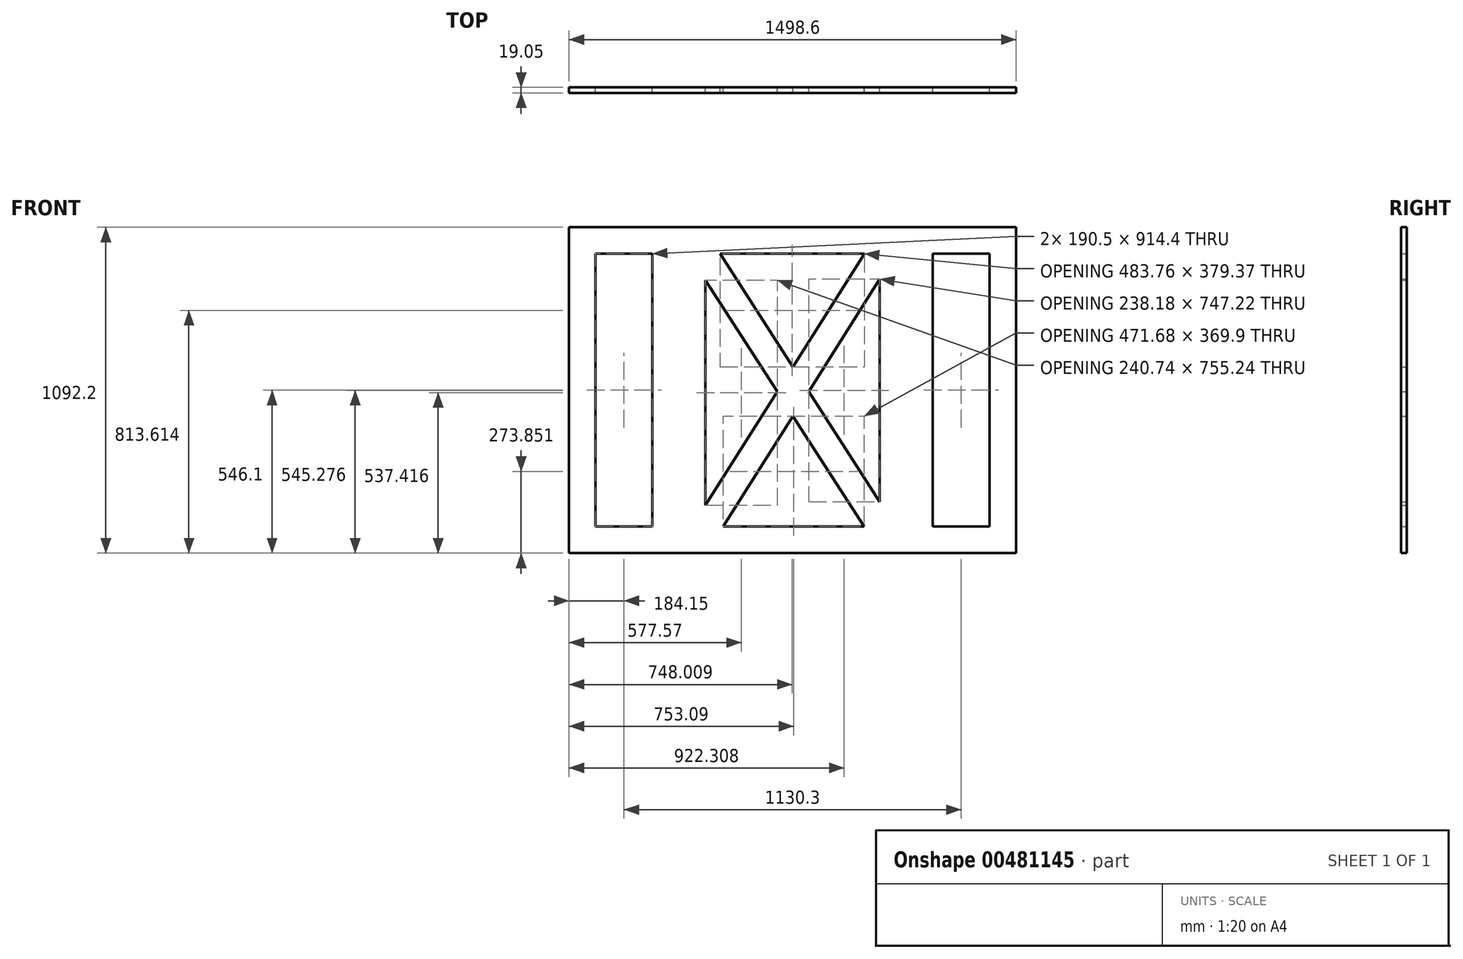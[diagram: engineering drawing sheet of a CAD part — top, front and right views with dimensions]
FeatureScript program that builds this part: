
annotation { "Feature Type Name" : "Feature", "Feature Type Description" : "" }
export const myFeature = defineFeature(function(context is Context, id is Id, definition is map)
    precondition{}
    {
        {
            var Q0;
            Q0=qCreatedBy(makeId("Front.planeOp"),FACE);
            var sketch = newSketch(context, id + "F0", { "sketchPlane" : qUnion([Q0])});
            skPoint(sketch, "E0.middle", {"position": v(0, 0) * mm});
            skLineSegment(sketch, "E1", {"start": v(-749.3, 546.1) * mm, "end": v(-749.3, -546.1) * mm});
            skLineSegment(sketch, "E2", {"start": v(-381, 546.1) * mm, "end": v(-381, -546.1) * mm});
            skLineSegment(sketch, "E3", {"start": v(749.3, 546.1) * mm, "end": v(749.3, -546.1) * mm});
            skLineSegment(sketch, "E4", {"start": v(381, 546.1) * mm, "end": v(381, -546.1) * mm});
            skLineSegment(sketch, "E5.bottom", {"start": v(-660.4, 457.2) * mm, "end": v(-469.9, 457.2) * mm});
            skLineSegment(sketch, "E5.top", {"start": v(-660.4, -457.2) * mm, "end": v(-469.9, -457.2) * mm});
            skLineSegment(sketch, "E5.left", {"start": v(-660.4, 457.2) * mm, "end": v(-660.4, -457.2) * mm});
            skLineSegment(sketch, "E5.right", {"start": v(-469.9, 457.2) * mm, "end": v(-469.9, -457.2) * mm});
            skLineSegment(sketch, "E6.MirrorCS", {"start": v(660.4, 457.2) * mm, "end": v(469.9, 457.2) * mm});
            skLineSegment(sketch, "E7.MirrorCS", {"start": v(660.4, 457.2) * mm, "end": v(660.4, -457.2) * mm});
            skLineSegment(sketch, "E8.MirrorCS", {"start": v(660.4, -457.2) * mm, "end": v(469.9, -457.2) * mm});
            skLineSegment(sketch, "E9.MirrorCS", {"start": v(469.9, 457.2) * mm, "end": v(469.9, -457.2) * mm});
            skLineSegment(sketch, "E10.bottom", {"start": v(-292.1, 457.2) * mm, "end": v(292.1, 457.2) * mm});
            skLineSegment(sketch, "E10.top", {"start": v(-292.1, -457.2) * mm, "end": v(292.1, -457.2) * mm});
            skLineSegment(sketch, "E10.left", {"start": v(-292.1, 457.2) * mm, "end": v(-292.1, -457.2) * mm});
            skLineSegment(sketch, "E10.right", {"start": v(292.1, 457.2) * mm, "end": v(292.1, -457.2) * mm});
            skLineSegment(sketch, "E11.0", {"start": v(-243.17, 457.2) * mm, "end": v(292.1, -374.43) * mm});
            skLineSegment(sketch, "E12.0", {"start": v(-292.1, 368.94) * mm, "end": v(239.63, -457.2) * mm});
            skLineSegment(sketch, "E13.0", {"start": v(240.59, 457.2) * mm, "end": v(-292.1, -386.3) * mm});
            skLineSegment(sketch, "E14.0", {"start": v(292.1, 372.79) * mm, "end": v(-232.05, -457.2) * mm});
            skLineSegment(sketch, "E15", {"start": v(-749.3, 546.1) * mm, "end": v(749.3, 546.1) * mm});
            skLineSegment(sketch, "E16", {"start": v(-749.3, -546.1) * mm, "end": v(749.3, -546.1) * mm});
            skSolve(sketch);
        }
        {
            var Q0;
            Q0 = qSketchRegion(id + "F0", true);
            var Q1;
            {var subQ1=sQuery(id+"F0.wireOp",EDGE,"E10.bottom");var subQ5=sQuery(id+"F0.wireOp",EDGE,"E10.left");var subQ6=makeQuery(id+"F0.imprint","INTERSECT",VERTEX,{"derivedFrom":[subQ1,subQ5]});Q1=makeQuery(id+"F0.imprint","IMPRINT",FACE,{"disambiguationData":[TD([[makeQuery(id+"F0.imprint","IMPRINT",EDGE,{"disambiguationData":[TD([[subQ6,-1.0]])],"derivedFrom":subQ1}),-1.0]])]});}
            var Q2;
            {var subQ1=sQuery(id+"F0.wireOp",EDGE,"E10.bottom");var subQ7=sQuery(id+"F0.wireOp",EDGE,"E10.right");var subQ8=makeQuery(id+"F0.imprint","INTERSECT",VERTEX,{"derivedFrom":[subQ1,subQ7]});Q2=makeQuery(id+"F0.imprint","IMPRINT",FACE,{"disambiguationData":[TD([[makeQuery(id+"F0.imprint","IMPRINT",EDGE,{"disambiguationData":[TD([[subQ8,1.0]])],"derivedFrom":subQ1}),-1.0]])]});}
            var Q3;
            {var subQ0=sQuery(id+"F0.wireOp",EDGE,"E13.0");var subQ1=sQuery(id+"F0.wireOp",EDGE,"E11.0");var subQ2=makeQuery(id+"F0.imprint","INTERSECT",VERTEX,{"derivedFrom":[subQ1,subQ0]});Q3=makeQuery(id+"F0.imprint","IMPRINT",FACE,{"disambiguationData":[TD([[makeQuery(id+"F0.imprint","IMPRINT",EDGE,{"disambiguationData":[TD([[subQ2,-1.0]])],"derivedFrom":subQ1}),-1.0]])]});}
            var Q4;
            {var subQ1=sQuery(id+"F0.wireOp",EDGE,"E10.left");var subQ7=sQuery(id+"F0.wireOp",EDGE,"E10.top");var subQ8=makeQuery(id+"F0.imprint","INTERSECT",VERTEX,{"derivedFrom":[subQ7,subQ1]});Q4=makeQuery(id+"F0.imprint","IMPRINT",FACE,{"disambiguationData":[TD([[makeQuery(id+"F0.imprint","IMPRINT",EDGE,{"disambiguationData":[TD([[subQ8,-1.0]])],"derivedFrom":subQ7}),1.0]])]});}
            var Q5;
            {var subQ1=sQuery(id+"F0.wireOp",EDGE,"E10.top");var subQ6=sQuery(id+"F0.wireOp",EDGE,"E10.right");var subQ9=makeQuery(id+"F0.imprint","INTERSECT",VERTEX,{"derivedFrom":[subQ1,subQ6]});Q5=makeQuery(id+"F0.imprint","IMPRINT",FACE,{"disambiguationData":[TD([[makeQuery(id+"F0.imprint","IMPRINT",EDGE,{"disambiguationData":[TD([[subQ9,1.0]])],"derivedFrom":subQ1}),1.0]])]});}
            extrude(context, id + "F1", {"entities" : qUnion([Q0, Q1, Q2, Q3, Q4, Q5]), "depth" : 19.05 * mm, "offsetDistance" : 25.4 * mm});
        }
    });
